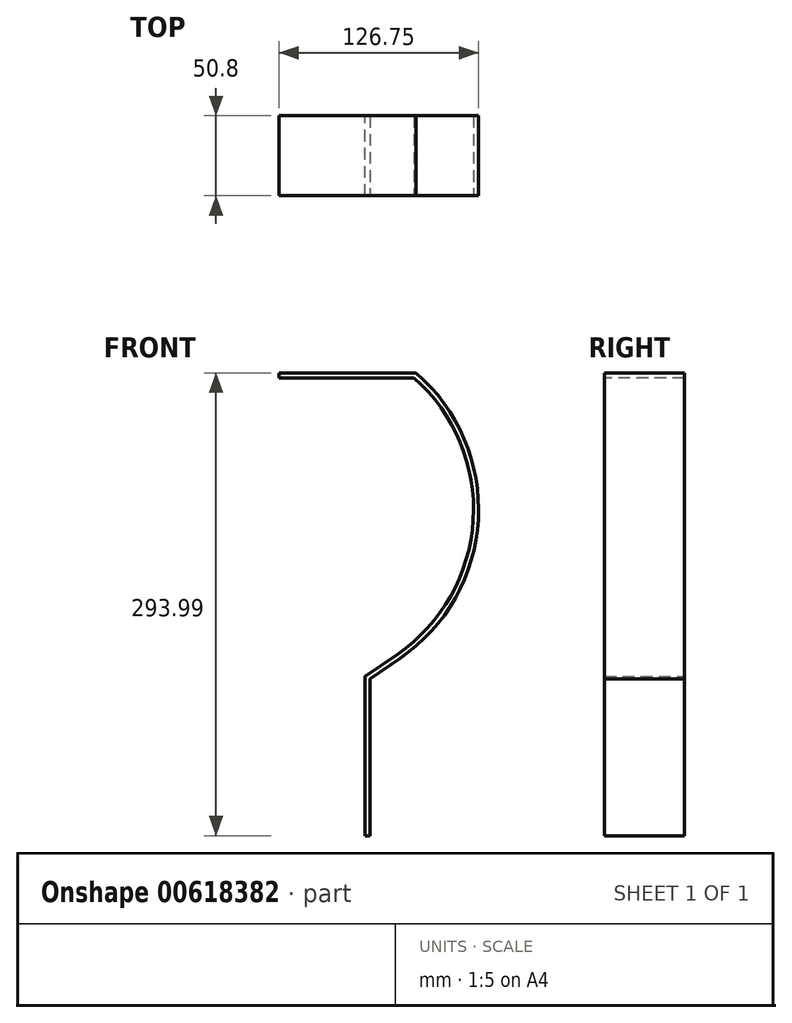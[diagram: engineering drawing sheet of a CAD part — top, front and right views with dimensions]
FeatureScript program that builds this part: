
annotation { "Feature Type Name" : "Feature", "Feature Type Description" : "" }
export const myFeature = defineFeature(function(context is Context, id is Id, definition is map)
    precondition{}
    {
        {
            var Q0;
            Q0=qCreatedBy(makeId("Top.planeOp"),FACE);
            var sketch = newSketch(context, id + "F0", { "sketchPlane" : qUnion([Q0])});
            skLineSegment(sketch, "E0.bottom", {"start": v(3.17, 50.8) * mm, "end": v(0, 50.8) * mm});
            skLineSegment(sketch, "E0.top", {"start": v(3.18, 0) * mm, "end": v(0, 0) * mm});
            skLineSegment(sketch, "E0.left", {"start": v(3.17, 50.8) * mm, "end": v(3.18, 0) * mm});
            skLineSegment(sketch, "E0.right", {"start": v(0, 50.8) * mm, "end": v(0, 0) * mm});
            skSolve(sketch);
        }
        {
            var Q0;
            Q0=qCreatedBy(makeId("Front.planeOp"),FACE);
            var sketch = newSketch(context, id + "F1", { "sketchPlane" : qUnion([Q0])});
            skLineSegment(sketch, "E1", {"start": v(47.4, 0) * mm, "end": v(47.4, 76.2) * mm});
            skArc(sketch, "E2", {"start": v(47.4, 76.2) * mm, "mid": v(116.35, 207.2) * mm, "end": v(47.4, 338.21) * mm});
            skLineSegment(sketch, "E3", {"start": v(47.4, 338.21) * mm, "end": v(-54.62, 338.21) * mm});
            skSolve(sketch);
        }
        {
            var Q0;
            Q0=makeQuery(id+"F0.imprint","IMPRINT",FACE,{"disambiguationData":[TD([[makeQuery(id+"F0.imprint","IMPRINT",EDGE,{"derivedFrom":sQuery(id+"F0.wireOp",EDGE,"E0.bottom")}),1.0]])]});
            var Q1;
            Q1=sQuery(id+"F1.wireOp",EDGE,"E2");
            var Q2;
            Q2=sQuery(id+"F1.wireOp",EDGE,"E1");
            var Q3;
            Q3=sQuery(id+"F1.wireOp",EDGE,"E3");
            sweep(context, id + "F2", {"profiles" : qUnion([Q0]), "path" : qUnion([Q1, Q2, Q3])});
        }
    });
